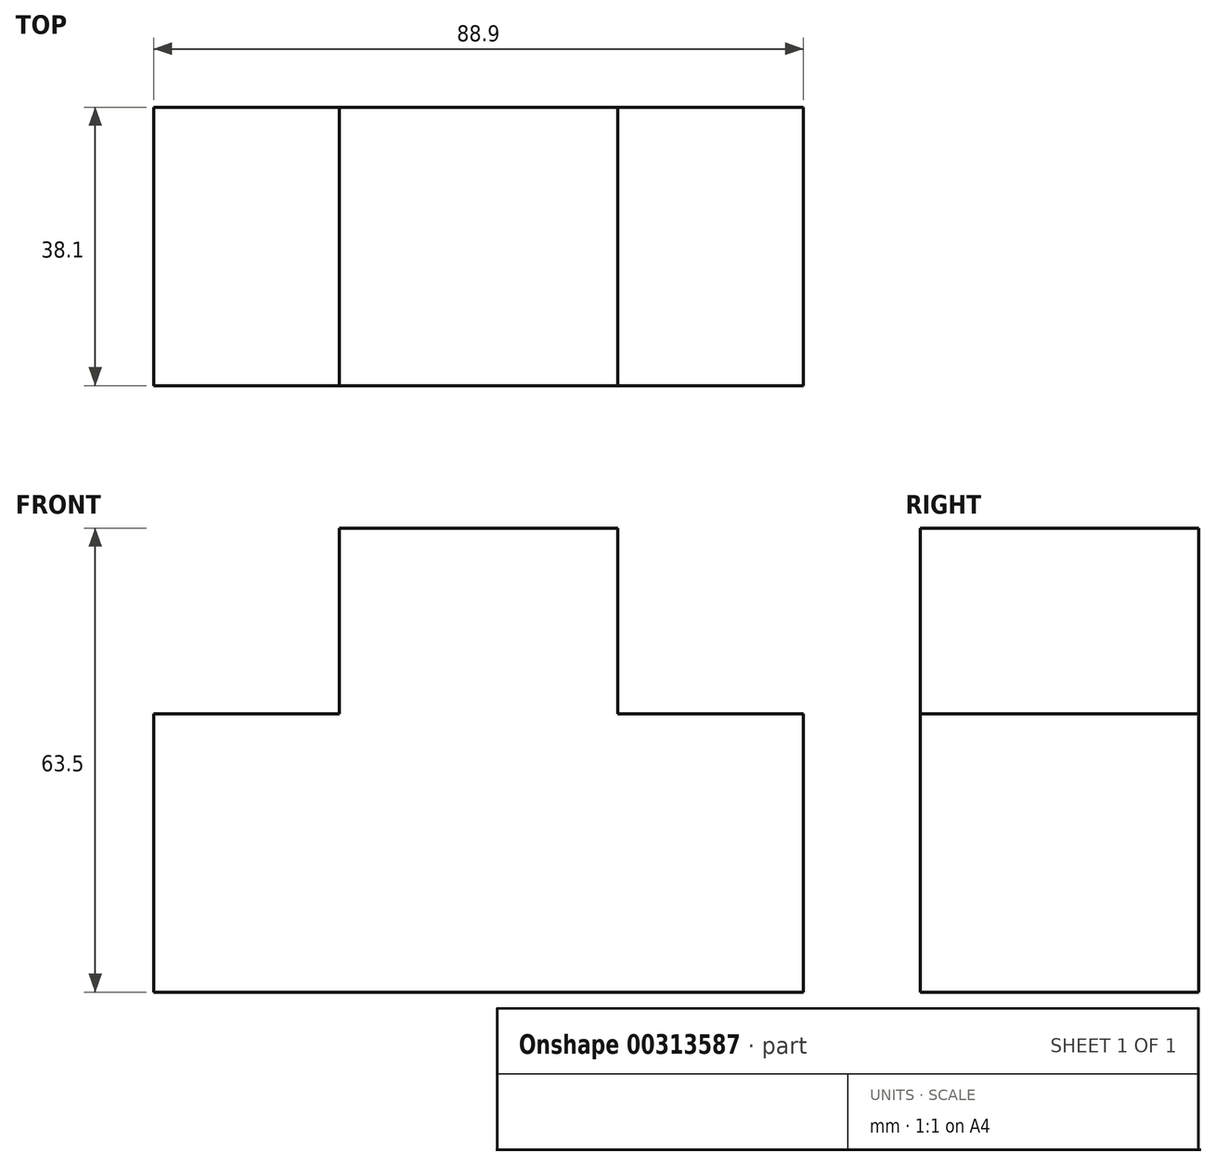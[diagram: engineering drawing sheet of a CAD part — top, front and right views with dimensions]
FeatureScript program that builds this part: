
annotation { "Feature Type Name" : "Feature", "Feature Type Description" : "" }
export const myFeature = defineFeature(function(context is Context, id is Id, definition is map)
    precondition{}
    {
        {
            var Q0;
            Q0=qCreatedBy(makeId("Front.planeOp"),FACE);
            var sketch = newSketch(context, id + "F0", { "sketchPlane" : qUnion([Q0])});
            skLineSegment(sketch, "E0", {"start": v(-94.18, -20.28) * mm, "end": v(-132.28, -20.28) * mm});
            skLineSegment(sketch, "E1", {"start": v(-94.18, -20.28) * mm, "end": v(-94.18, -45.68) * mm});
            skLineSegment(sketch, "E2", {"start": v(-94.18, -45.68) * mm, "end": v(-68.78, -45.68) * mm});
            skLineSegment(sketch, "E3", {"start": v(-68.78, -45.68) * mm, "end": v(-68.78, -83.78) * mm});
            skLineSegment(sketch, "E4", {"start": v(-68.78, -83.78) * mm, "end": v(-157.68, -83.78) * mm});
            skLineSegment(sketch, "E5", {"start": v(-157.68, -83.78) * mm, "end": v(-157.68, -45.68) * mm});
            skLineSegment(sketch, "E6", {"start": v(-157.68, -45.68) * mm, "end": v(-132.28, -45.68) * mm});
            skLineSegment(sketch, "E7", {"start": v(-132.28, -45.68) * mm, "end": v(-132.28, -20.28) * mm});
            skSolve(sketch);
        }
        {
            var Q0;
            Q0=makeQuery(id+"F0.imprint","IMPRINT",FACE,{"disambiguationData":[TD([[makeQuery(id+"F0.imprint","IMPRINT",EDGE,{"derivedFrom":sQuery(id+"F0.wireOp",EDGE,"E0")}),1.0]])]});
            extrude(context, id + "F1", {"entities" : qUnion([Q0]), "depth" : 38.1 * mm});
        }
    });
